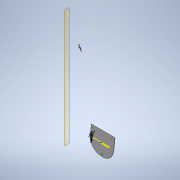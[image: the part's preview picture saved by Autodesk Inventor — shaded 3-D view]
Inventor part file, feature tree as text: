
AUTODESK INVENTOR PART (.ipt)
format: ipt  version: 2022 (Build 260153000, 153)  size: 4,051,968 bytes
history: native  units: mm
features: sketch x30, extrude x24, fillet x17, chamfer x10, other x2
ambient origin geometry x8: Origin, YZ Plane, XZ Plane, XY Plane, X Axis, Y Axis, Z Axis, Center Point
bodies: Solid1 (feature_tree)
feature tree (83):
  extrude  "Extrusion1"  Depth=0.698132mm
  sketch  "Sketch2"  dims[d52=15.0mm d53=0.0mm d54=13.0mm]
  extrude  "Extrusion2"  Depth=13.0mm
  chamfer  "Chamfer1"  [1 undecoded]
  sketch  "Sketch4"  dims[d56=265.0mm d57=0.0mm d58=0.0mm]
  extrude  "Extrusion3"  Depth=20.0mm
  extrude  "Extrusion4"  Depth=52.15mm
  extrude  "Extrusion5"  Depth=82.0mm
  sketch  "Sketch6"  dims[d63=52.15mm d64=52.15mm]
  extrude  "Extrusion6"  Depth=10.0mm
  extrude  "Extrusion7"  Depth=10.0mm TaperAngle=0.0deg
  chamfer  "Chamfer2"  Distance=11.0mm
  extrude  "Extrusion8"  Depth=8.0mm TaperAngle=0.0deg
  chamfer  "Chamfer3"  [1 undecoded]
  extrude  "Extrusion9"  Depth=55.0mm TaperAngle=0.0deg
  fillet  "Fillet2"  Radius=1.0mm
  fillet  "Fillet3"  Radius=26.5mm
  fillet  "Fillet4"  Radius=33.0mm
  extrude  "Extrusion10"  Depth=1.2mm
  chamfer  "Chamfer4"  Distance=9.0mm
  sketch  "Sketch10"  dims[d74=15.0mm d75=8.0mm d76=0.0mm]
  extrude  "Extrusion11"  Depth=33.0mm
  fillet  "Fillet6"  Radius=3.0mm
  fillet  "Fillet7"  [1 undecoded]
  extrude  "Extrusion12"  Depth=25.0mm TaperAngle=0.0deg
  fillet  "Fillet8"  Radius=0.5mm
  fillet  "Fillet9"  Radius=1.0mm
  sketch  "Sketch13"  dims[d81=5.0mm d82=55.0mm d83=0.0mm]
  extrude  "Extrusion13"  Depth=0.5mm
  sketch  "Sketch15"  dims[d90=0.25mm d91=2.0mm d92=45.0deg d93=26.5mm d94=33.0mm]
  fillet  "Fillet10"  Radius=4.0mm
  chamfer  "Chamfer5"  Distance=40.0mm
  extrude  "Extrusion14"  Depth=2.0mm TaperAngle=0.0deg
  fillet  "Fillet11"  Radius=0.5mm
  sketch  "Sketch17"  dims[d98=5.0mm]
  sketch  "Sketch18"  dims[d99=2.0mm]
  extrude  "Extrusion16"  Depth=0.5mm
  sketch  "Sketch22"  dims[d101=2.0mm]
  extrude  "Extrusion18"  TaperAngle=0.0deg  [1 undecoded]
  chamfer  "Chamfer8"  Distance=27.0mm
  extrude  "Extrusion20"  Depth=1.0mm TaperAngle=0.0deg
  extrude  "Extrusion21"  Depth=2.0mm
  chamfer  "Chamfer11"  Distance=1.0mm
  chamfer  "Chamfer12"  Distance=3.70509mm
  fillet  "Fillet18"  Radius=0.5mm
  fillet  "Fillet19"  Radius=0.5mm
  sketch  "Sketch26"  dims[d105=5.15mm]
  extrude  "Extrusion22"  TaperAngle=0.0deg  [1 undecoded]
  fillet  "Fillet21"  [1 undecoded]
  fillet  "Fillet22"  [1 undecoded]
  fillet  "Fillet23"  Radius=1.0mm
  extrude  "Extrusion23"  TaperAngle=0.0deg  [1 undecoded]
  fillet  "Fillet24"  Radius=19.0mm
  extrude  "Extrusion24"  Depth=5.5mm
  chamfer  "Chamfer13"  Distance=5.5mm
  sketch  "Sketch29"  dims[d108=7.15mm]
  sketch  "Sketch31"  dims[d110=18.0mm d111=9.0mm d112=0.0mm]
  sketch  "Sketch30"  dims[d109=61.0mm]
  extrude  "Extrusion25"  Depth=19.0mm
  extrude  "Extrusion26"  Depth=62.65mm
  extrude  "Extrusion27"  Depth=51.65mm
  chamfer  "Chamfer14"  Distance=21.0mm
  fillet  "Fillet26"  Radius=1.0mm
  fillet  "Fillet27"  Radius=0.5mm
  sketch  "Sketch1"  dims[d7=0.0mm d32=0.698132mm]
  other  "Image1"
  sketch  "Sketch3"  dims[d55=75.0mm]
  sketch  "Sketch5"  dims[d59=2.0mm d60=2.0mm d61=45.0deg d62=20.0mm]
  sketch  "Sketch7"  dims[d65=21.25mm d66=82.0mm]
  sketch  "Sketch8"  dims[d67=8.0mm d68=10.0mm]
  sketch  "Sketch9"  dims[d69=2.0mm d70=10.0mm d71=0.0mm d72=11.0mm d73=0.0mm]
  other  "Image2"
  sketch  "Sketch11"  dims[d77=4.0mm]
  sketch  "Sketch12"  dims[d78=1.0mm d79=0.0mm d80=0.0mm]
  sketch  "Sketch14"  dims[d84=5.0mm d85=2.0mm d86=45.0deg d88=1.0mm d89=0.0mm]
  sketch  "Sketch16"  dims[d95=6.0mm d96=0.0mm d97=1.2mm]
  sketch  "Sketch20"  dims[d100=0.5mm]
  sketch  "Sketch23"  dims[d102=5.15mm]
  sketch  "Sketch24"  dims[d103=90.0mm]
  sketch  "Sketch25"  dims[d104=272.0mm]
  sketch  "Sketch27"  dims[d106=35.0mm]
  sketch  "Sketch28"  dims[d107=2.0mm]
  sketch  "Sketch32"  dims[d113=0.5mm d114=2.0mm d115=45.0deg d124=33.0mm d141=3.0mm d143=90.0deg d144=25.0mm d145=2.0mm d146=0.0mm d147=0.0mm d148=0.5mm d149=1.0mm d150=0.5mm d151=4.0mm d152=40.0mm d153=2.0mm d154=0.0mm d155=0.5mm d156=0.5mm d157=0.0mm d158=27.0mm d159=1.0mm d160=0.0mm d161=2.0mm d162=1.0mm d163=3.70509mm d164=0.5mm d165=0.5mm d166=2.0mm d167=45.0deg d168=0.0mm d169=0.0mm d170=0.0mm d171=1.0mm d172=0.0mm d173=19.0mm d174=5.5mm d175=5.5mm d176=19.0mm d177=62.65mm d178=51.65mm d179=21.0mm d180=1.0mm d181=0.0mm d183=0.5mm d184=8.0mm d195=7.0mm d196=8.0mm d197=4.0mm d198=25.0mm d199=0.0mm d213=3.0mm d214=17.6mm d216=32.75mm d217=1.9mm d218=5.0mm d219=4.0mm d220=0.0mm d221=2.0mm d222=2.0mm d223=45.0deg d224=4.0mm d225=2.0mm d226=32.75mm d229=10.0mm d230=0.0mm d233=0.0mm d234=10.0mm d235=0.0mm d242=3.0mm d243=1.5mm d244=45.0deg d245=3.0mm d246=1.5mm d247=45.0deg d248=0.5mm d249=1.0mm d250=1.5mm d251=5.0mm d252=0.0mm d254=0.0mm d255=0.0mm d256=0.5mm d257=0.5mm d258=0.5mm d259=0.0mm d260=0.0mm d261=125.0mm d263=2.85mm d264=5.0mm d265=26.075mm d266=26.075mm d267=6.0mm d268=2.85mm d269=5.0mm d270=2.85mm d271=3.0mm d272=5.0mm d273=5.0mm d274=10.0mm d275=0.0mm d276=0.5mm d277=1.0mm d278=45.0deg d279=15.25mm d280=3.0mm d281=8.0mm d283=0.0mm d284=0.0mm d285=3.0mm d286=0.0mm d287=7.0mm d288=1.6mm d289=0.0mm d290=4.5mm d291=3.0mm d292=45.0deg d293=2.0mm d294=1.0mm d87=0.0mm]
note: 8 required parameter values undecoded (feature->parameter linkage not recoverable at this tier; creation-order binding heuristic only, values carry confidence <= 0.55)
